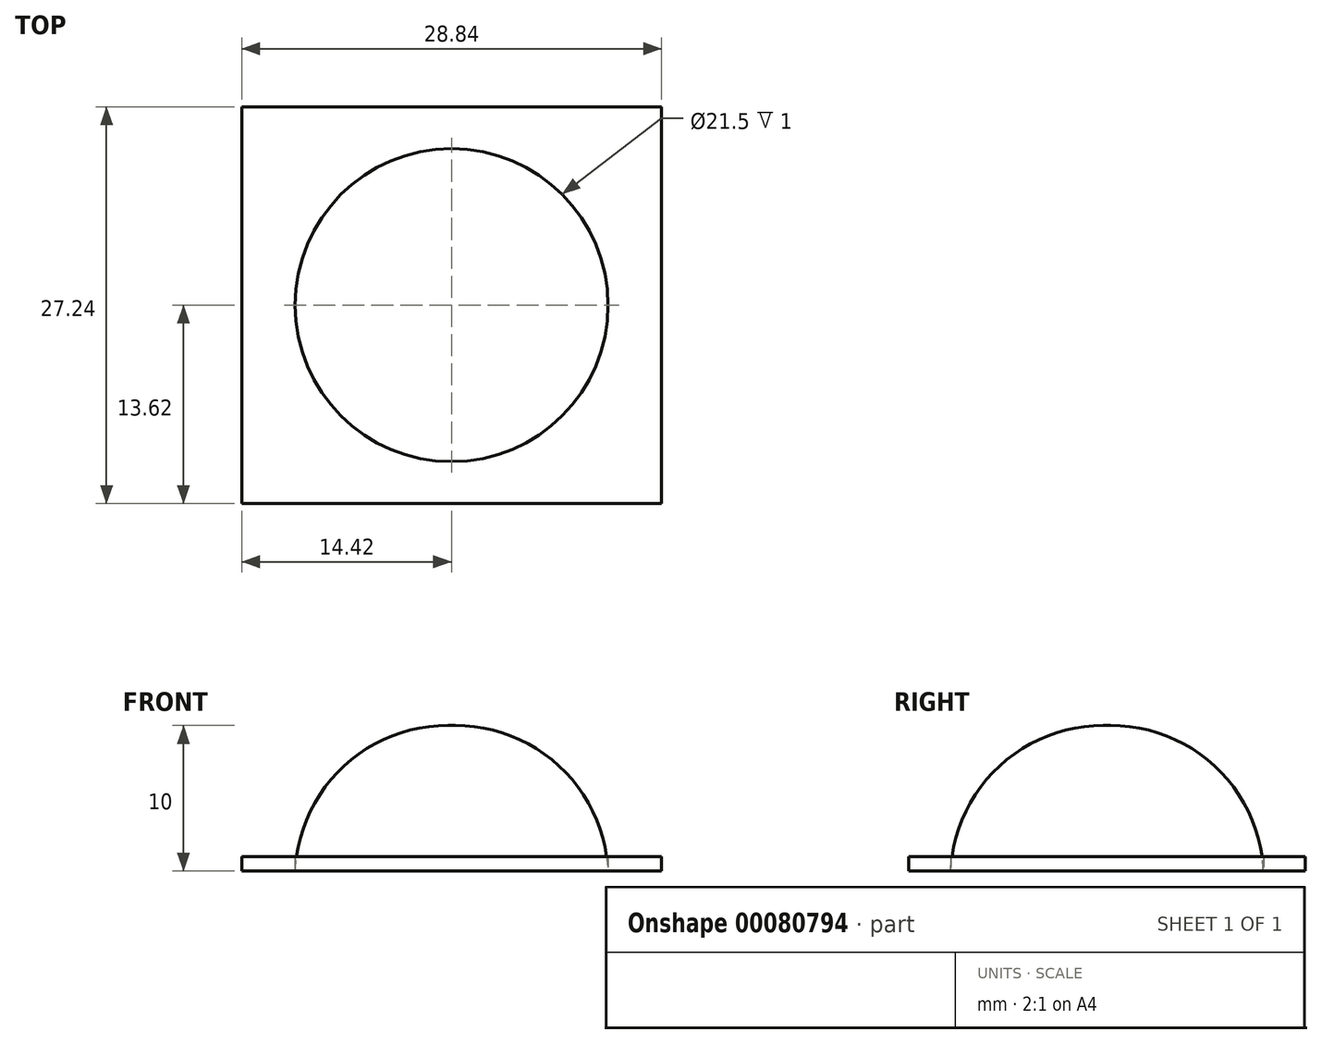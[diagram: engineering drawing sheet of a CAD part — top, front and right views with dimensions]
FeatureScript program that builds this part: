
annotation { "Feature Type Name" : "Feature", "Feature Type Description" : "" }
export const myFeature = defineFeature(function(context is Context, id is Id, definition is map)
    precondition{}
    {
        {
            var Q0;
            Q0=qCreatedBy(makeId("Top.planeOp"),FACE);
            var sketch = newSketch(context, id + "F0", { "sketchPlane" : qUnion([Q0])});
            skCircle(sketch, "E0", {"center": v(0, 0) * mm, "radius": 10.75 * mm});
            skLineSegment(sketch, "E1.bottom", {"start": v(14.42, -13.62) * mm, "end": v(-14.42, -13.62) * mm});
            skLineSegment(sketch, "E1.top", {"start": v(14.42, 13.62) * mm, "end": v(-14.42, 13.62) * mm});
            skLineSegment(sketch, "E1.left", {"start": v(14.42, -13.62) * mm, "end": v(14.42, 13.62) * mm});
            skLineSegment(sketch, "E1.right", {"start": v(-14.42, -13.62) * mm, "end": v(-14.42, 13.62) * mm});
            skSolve(sketch);
        }
        {
            var Q0;
            Q0=makeQuery(id+"F0.imprint","IMPRINT",FACE,{"disambiguationData":[TD([[makeQuery(id+"F0.imprint","IMPRINT",EDGE,{"derivedFrom":sQuery(id+"F0.wireOp",EDGE,"E0")}),1.0]])]});
            extrude(context, id + "F1", {"entities" : qUnion([Q0]), "depth" : 10 * mm, "hasDraft" : true, "draftAngle" : 3 * degree});
        }
        {
            var Q0;
            Q0=makeQuery(id+"F1.opExtrude","CAP_EDGE",EDGE,{"disambiguationData":[OSD([sQuery(id+"F0.wireOp",EDGE,"E0")])],"isStart":false});
            fillet(context, id + "F2", {"entities" : qUnion([Q0]), "radius" : 10.5 * mm, "tangentPropagation" : true, "allowEdgeOverflow" : false});
        }
        {
            var Q0;
            Q0 = qSketchRegion(id + "F0", true);
            var sketch = newSketch(context, id + "F3", { "sketchPlane" : qUnion([Q0])});
            skSolve(sketch);
        }
        {
            var Q0;
            Q0 = qSketchRegion(id + "F3", true);
            var Q1;
            Q1=makeQuery(id+"F3.imprint","IMPRINT",FACE,{"disambiguationData":[TD([[makeQuery(id+"F3.imprint","IMPRINT",EDGE,{"derivedFrom":makeQuery(id+"F0.imprint","IMPRINT",EDGE,{"derivedFrom":sQuery(id+"F0.wireOp",EDGE,"E0")})}),-1.0]])]});
            extrude(context, id + "F4", {"entities" : qUnion([Q0, Q1]), "depth" : 1 * mm});
        }
    });
